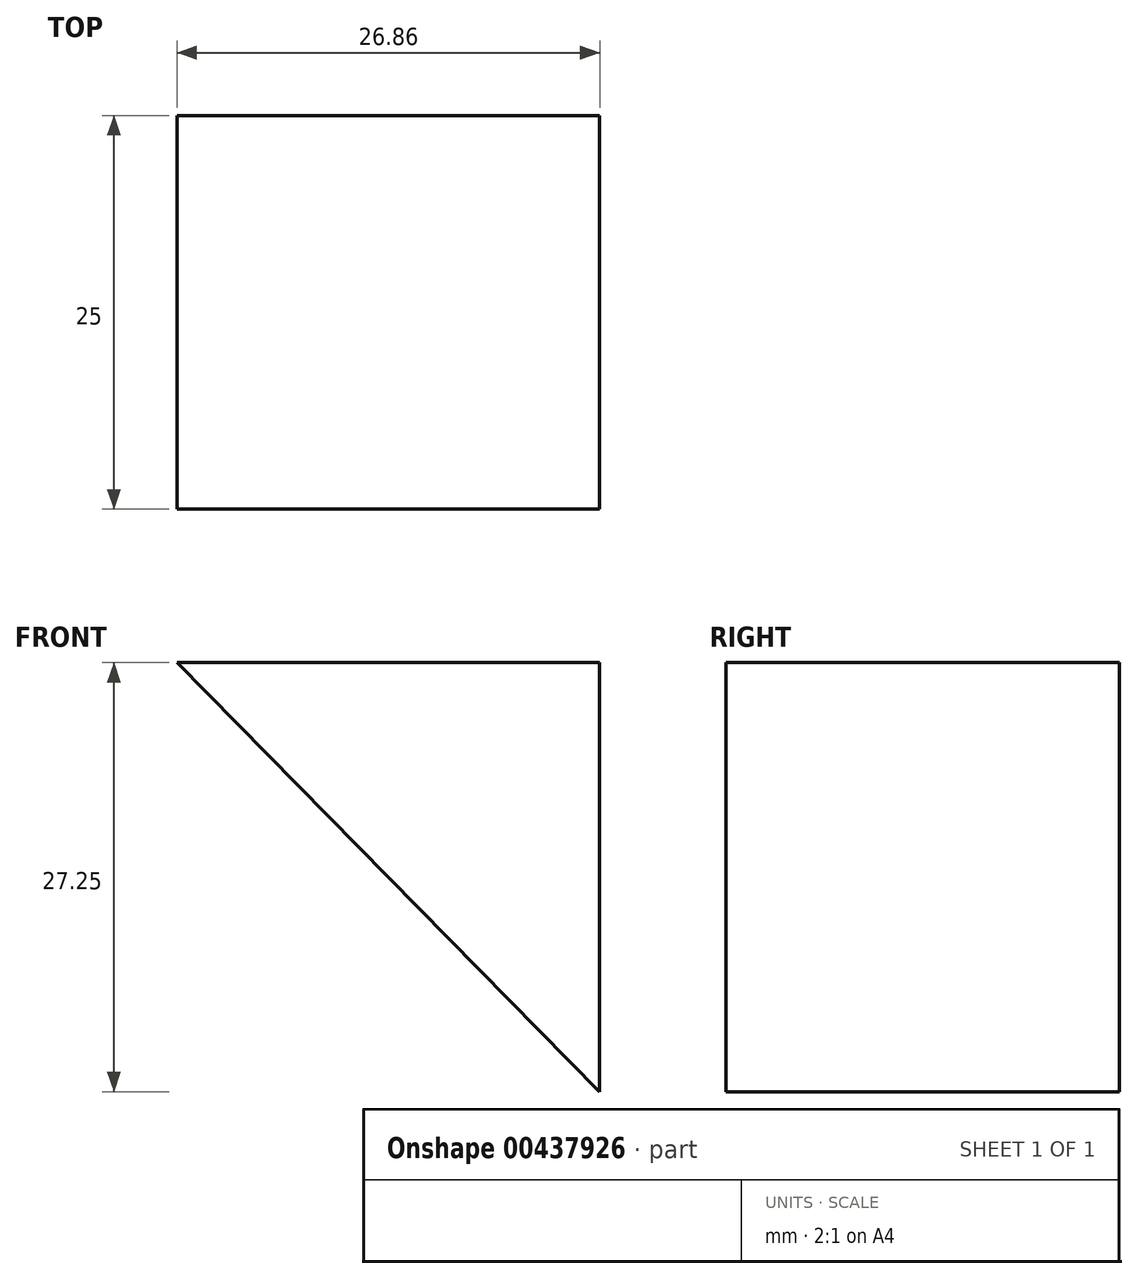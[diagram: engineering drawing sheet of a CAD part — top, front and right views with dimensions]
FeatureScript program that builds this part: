
annotation { "Feature Type Name" : "Feature", "Feature Type Description" : "" }
export const myFeature = defineFeature(function(context is Context, id is Id, definition is map)
    precondition{}
    {
        {
            var Q0;
            Q0=qCreatedBy(makeId("Front.planeOp"),FACE);
            var sketch = newSketch(context, id + "F0", { "sketchPlane" : qUnion([Q0])});
            skLineSegment(sketch, "E0", {"start": v(38.92, 19.45) * mm, "end": v(65.78, -7.8) * mm});
            skLineSegment(sketch, "E1", {"start": v(65.78, -7.8) * mm, "end": v(65.78, 19.45) * mm});
            skLineSegment(sketch, "E2", {"start": v(65.78, 19.45) * mm, "end": v(38.92, 19.45) * mm});
            skSolve(sketch);
        }
        {
            var Q0;
            Q0 = qSketchRegion(id + "F0", true);
            extrude(context, id + "F1", {"entities" : qUnion([Q0]), "depth" : 25 * mm});
        }
    });
